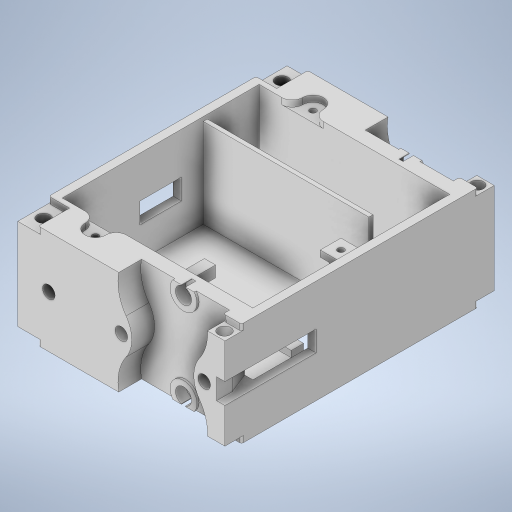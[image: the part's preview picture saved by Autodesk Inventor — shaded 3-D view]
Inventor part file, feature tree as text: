
AUTODESK INVENTOR PART (.ipt)
format: ipt  version: 2024 (Build 280153000, 153)  size: 842,240 bytes
history: native  units: in
note: dims shown in document units (in); Inventor stores cm internally (conversion verified against a paired STEP export)
features: extrude x22, sketch x21, projected_geometry x20, mirror x4, plane x2, chamfer x2, fillet x1
ambient origin geometry x8: Origin, YZ Plane, XZ Plane, XY Plane, X Axis, Y Axis, Z Axis, Center Point
bodies: Solid1 (feature_tree)
feature tree (72):
  extrude  "Extrusion1"  Depth=3.937in
  plane  "Work Plane1"
  plane  "Work Plane2"
  extrude  "Extrusion2"  TaperAngle=0.0deg  [1 undecoded]
  extrude  "Extrusion3"  Depth=2.3622in
  extrude  "Extrusion4"  Depth=0.3031in
  mirror  "Mirror1"
  extrude  "Extrusion5"  Depth=1.1811in
  mirror  "Mirror2"
  extrude  "Extrusion6"  Depth=1.6535in
  extrude  "Extrusion7"  Depth=0.0394in
  sketch  "Sketch9"  dims[d18=0.0787in d19=1.6535in]
  extrude  "Extrusion8"  Depth=1.6535in
  extrude  "Extrusion9"  Depth=1.1811in
  mirror  "Mirror3"
  mirror  "Mirror4"
  extrude  "Extrusion10"  Depth=0.8268in
  extrude  "Extrusion11"  Depth=0.0394in
  extrude  "Extrusion12"  Depth=0.7874in
  extrude  "Extrusion13"  Depth=0.3937in
  extrude  "Extrusion15"  Depth=0.1181in
  extrude  "Extrusion16"  Depth=0.315in
  extrude  "Extrusion17"  Depth=0.3937in
  extrude  "Extrusion18"  Depth=0.3937in
  extrude  "Extrusion19"  Depth=0.5906in
  extrude  "Extrusion20"  Depth=0.2362in
  extrude  "Extrusion21"  Depth=0.4331in
  extrude  "Extrusion22"  Depth=0.0394in
  extrude  "Extrusion23"  TaperAngle=0.0deg  [1 undecoded]
  chamfer  "Chamfer1"  Distance=3.622in
  fillet  "Fillet1"  Radius=3.7402in
  chamfer  "Chamfer2"  Distance=1.8701in
  sketch  "Sketch1"  dims[d0=1.9685in d1=3.937in]
  sketch  "Sketch3"  dims[d2=5.1181in d3=0.0in]
  projected_geometry  "Projected Loop1"
  sketch  "Sketch4"  dims[d4=1.1811in d5=2.3622in]
  projected_geometry  "Projected Loop2"
  sketch  "Sketch5"  dims[d6=1.6535in d7=0.3031in]
  projected_geometry  "Projected Loop3"
  sketch  "Sketch6"  dims[d8=0.8268in d11=1.1811in]
  projected_geometry  "Projected Loop4"
  projected_geometry  "Projected Loop5"
  sketch  "Sketch7"  dims[d12=0.5906in d13=0.0in d14=1.6535in]
  projected_geometry  "Projected Loop6"
  sketch  "Sketch8"  dims[d15=0.4331in d16=0.0in d17=0.0394in]
  projected_geometry  "Projected Loop7"
  projected_geometry  "Projected Loop8"
  projected_geometry  "Projected Loop9"
  sketch  "Sketch10"  dims[d20=0.8268in d21=1.1811in]
  projected_geometry  "Projected Loop10"
  sketch  "Sketch11"  dims[d22=0.5118in d23=0.8268in]
  projected_geometry  "Projected Loop11"
  sketch  "Sketch12"  dims[d24=0.0394in d25=0.0in d26=0.2362in]
  projected_geometry  "Projected Loop12"
  sketch  "Sketch13"  dims[d27=1.5748in d28=0.7874in]
  projected_geometry  "Projected Loop13"
  sketch  "Sketch15"  dims[d29=0.5906in d30=0.3937in]
  projected_geometry  "Projected Loop15"
  sketch  "Sketch16"  dims[d31=0.0in d32=0.1181in]
  sketch  "Sketch17"  dims[d33=0.1181in d34=0.315in]
  projected_geometry  "Projected Loop16"
  sketch  "Sketch18"  dims[d35=0.0in d36=0.3937in]
  projected_geometry  "Projected Loop17"
  sketch  "Sketch19"  dims[d37=0.3937in d38=0.1181in]
  projected_geometry  "Projected Loop18"
  sketch  "Sketch20"  dims[d39=0.1181in d40=0.5906in]
  projected_geometry  "Projected Loop19"
  sketch  "Sketch21"  dims[d41=0.0in d42=0.2362in]
  sketch  "Sketch22"  dims[d43=0.2362in d44=0.4331in]
  projected_geometry  "Projected Loop20"
  sketch  "Sketch23"  dims[d45=0.0in d46=0.1969in d47=0.0in d48=3.622in d49=3.7402in d50=1.8701in d51=1.7717in d52=0.0in d53=1.7323in d54=0.3937in d55=0.1969in d56=1.7717in d57=0.0in d58=0.9843in d59=0.9843in d60=0.1181in d61=0.1181in d62=4.1339in d63=2.0669in d64=0.315in d65=0.0in d66=0.3937in d67=0.1181in d68=0.0in d83=0.2126in d84=0.2126in d85=0.2126in d86=0.2126in d87=0.2126in d88=0.2126in d89=0.1181in d90=0.1181in d91=0.1181in d92=1.3622in d93=2.1496in d94=2.1496in d95=0.5512in d96=0.0in d97=0.3937in d98=0.1969in d99=0.3543in d100=0.0787in d101=0.3937in d102=0.0in d103=0.1181in d104=0.2362in d105=0.3937in d106=0.0in d107=0.1181in d108=0.3937in d109=0.0in d110=0.0787in d111=0.6102in d112=1.6929in d113=0.0in d114=0.3937in d115=0.5906in d116=0.0787in d117=1.6929in d118=0.0in d119=0.6299in d120=0.4724in d121=0.315in d122=0.5906in d123=0.0in d124=0.0in d125=0.2362in d126=0.1181in d127=0.1181in d128=0.0984in d129=0.0984in d130=0.1181in d131=0.0in d132=0.7874in d133=0.3937in d134=0.1181in d135=0.0in d136=0.1575in d137=0.3937in d138=45.0deg d139=0.0394in d140=0.2362in d141=0.0787in d142=45.0deg]
  projected_geometry  "Projected Loop21"
note: 2 required parameter values undecoded (feature->parameter linkage not recoverable at this tier; creation-order binding heuristic only, values carry confidence <= 0.55)
